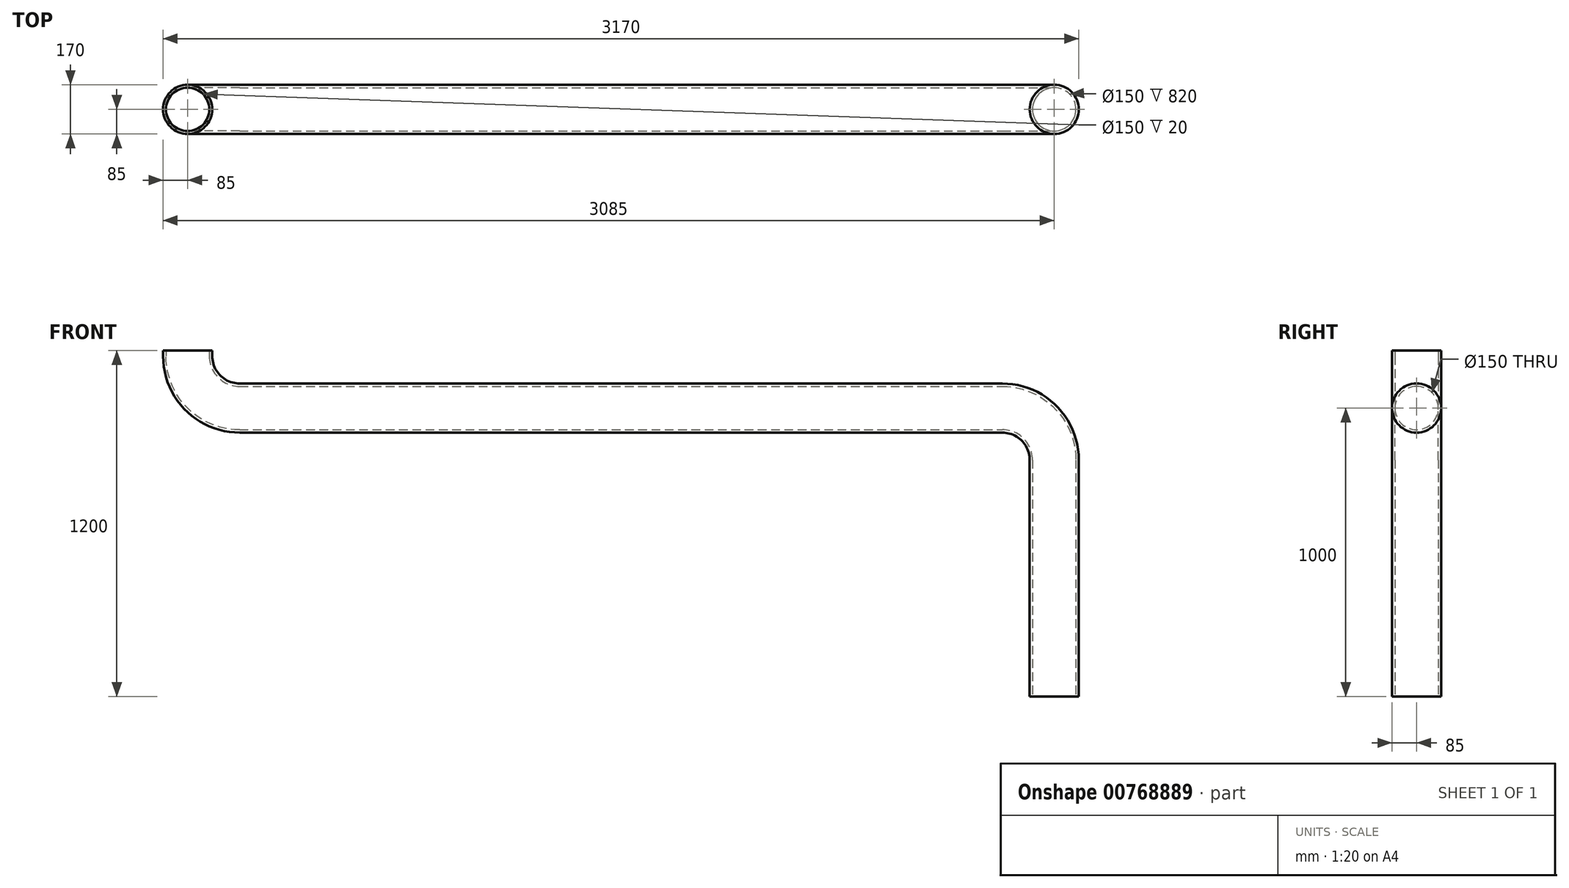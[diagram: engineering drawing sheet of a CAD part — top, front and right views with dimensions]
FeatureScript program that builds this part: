
annotation { "Feature Type Name" : "Feature", "Feature Type Description" : "" }
export const myFeature = defineFeature(function(context is Context, id is Id, definition is map)
    precondition{}
    {
        {
            var Q0;
            Q0=qCreatedBy(makeId("Front.planeOp"),FACE);
            var sketch = newSketch(context, id + "F0", { "sketchPlane" : qUnion([Q0])});
            skLineSegment(sketch, "E0", {"start": v(0, 0) * mm, "end": v(0, -20) * mm});
            skLineSegment(sketch, "E1", {"start": v(180, -200) * mm, "end": v(2820, -200) * mm});
            skLineSegment(sketch, "E2", {"start": v(3000, -380) * mm, "end": v(3000, -1200) * mm});
            skPoint(sketch, "E3.visualSharp", {"position": v(0, -200) * mm});
            skArc(sketch, "E3.filletArc", {"start": v(0, -20) * mm, "mid": v(52.72, -147.28) * mm, "end": v(180, -200) * mm});
            skPoint(sketch, "E4.visualSharp", {"position": v(3000, -200) * mm});
            skArc(sketch, "E4.filletArc", {"start": v(3000, -380) * mm, "mid": v(2947.28, -252.72) * mm, "end": v(2820, -200) * mm});
            skSolve(sketch);
        }
        {
            var Q0;
            Q0=qCreatedBy(makeId("Top.planeOp"),FACE);
            var sketch = newSketch(context, id + "F1", { "sketchPlane" : qUnion([Q0])});
            skCircle(sketch, "E5", {"center": v(0, 0) * mm, "radius": 75 * mm});
            skCircle(sketch, "E6", {"center": v(0, 0) * mm, "radius": 85 * mm});
            skSolve(sketch);
        }
        {
            var Q0;
            Q0=makeQuery(id+"F1.imprint","IMPRINT",FACE,{"disambiguationData":[TD([[makeQuery(id+"F1.imprint","IMPRINT",EDGE,{"derivedFrom":sQuery(id+"F1.wireOp",EDGE,"E5")}),-1.0]])]});
            var Q1;
            Q1=sQuery(id+"F0.wireOp",EDGE,"E0");
            var Q2;
            Q2=sQuery(id+"F0.wireOp",EDGE,"E3.filletArc");
            var Q3;
            Q3=sQuery(id+"F0.wireOp",EDGE,"E1");
            var Q4;
            Q4=sQuery(id+"F0.wireOp",EDGE,"E4.filletArc");
            var Q5;
            Q5=sQuery(id+"F0.wireOp",EDGE,"E2");
            sweep(context, id + "F2", {"profiles" : qUnion([Q0]), "path" : qUnion([Q1, Q2, Q3, Q4, Q5])});
        }
    });
